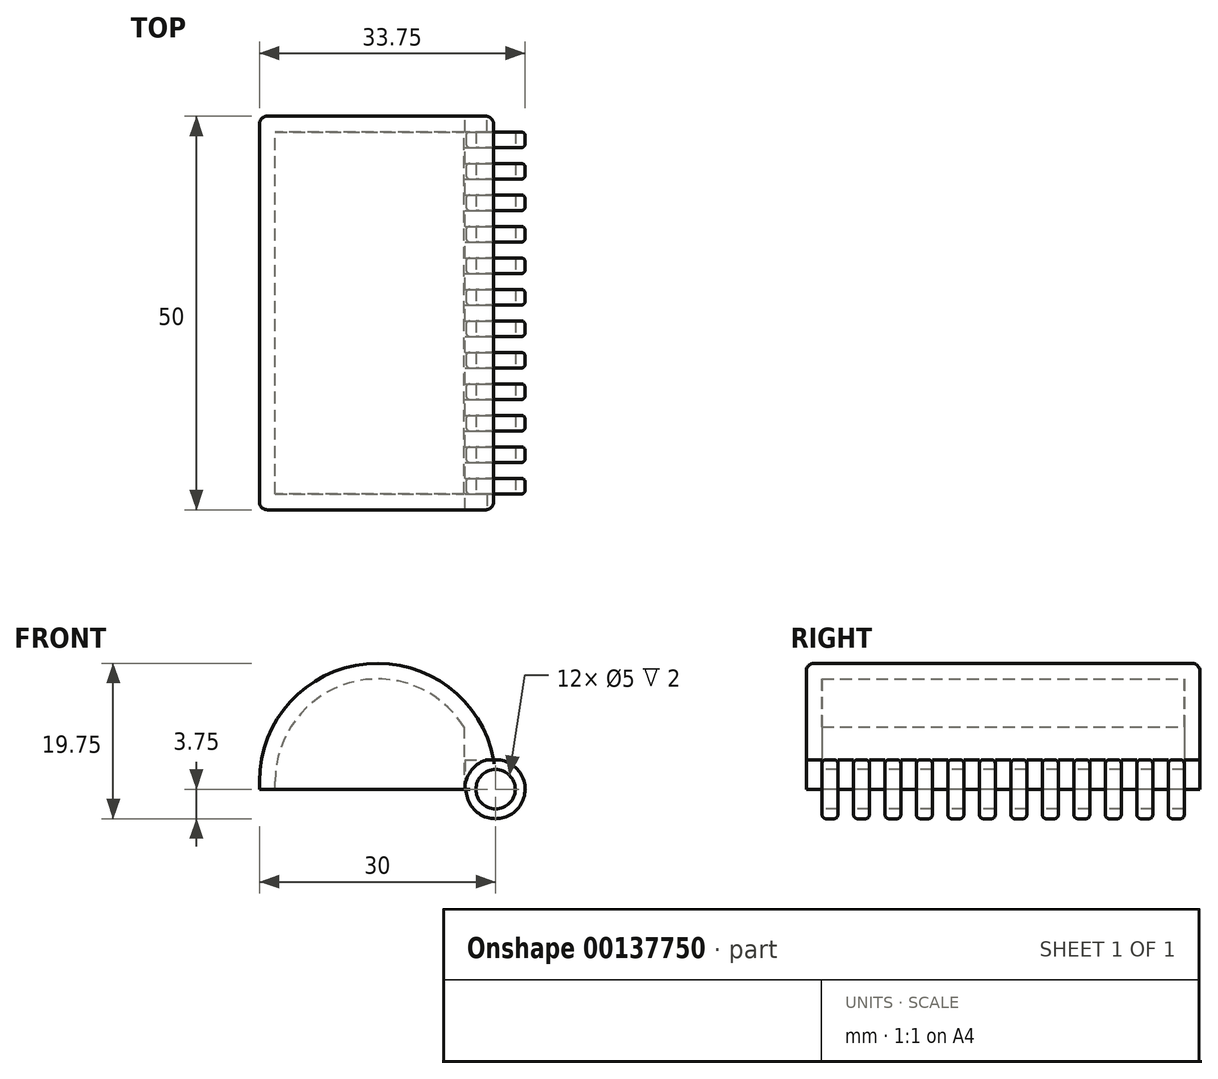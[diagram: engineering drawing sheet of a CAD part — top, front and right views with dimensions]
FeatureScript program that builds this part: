
annotation { "Feature Type Name" : "Feature", "Feature Type Description" : "" }
export const myFeature = defineFeature(function(context is Context, id is Id, definition is map)
    precondition{}
    {
        {
            var Q0;
            Q0=qCreatedBy(makeId("Front.planeOp"),FACE);
            var sketch = newSketch(context, id + "F0", { "sketchPlane" : qUnion([Q0])});
            skLineSegment(sketch, "E0.bottom", {"start": v(-15, 0) * mm, "end": v(15, 0) * mm});
            skLineSegment(sketch, "E0.left", {"start": v(-15, 0) * mm, "end": v(-15, 1) * mm});
            skLineSegment(sketch, "E0.right", {"start": v(15, 0) * mm, "end": v(15, 1) * mm});
            skArc(sketch, "E1", {"start": v(15, 1) * mm, "mid": v(0, 16) * mm, "end": v(-15, 1) * mm});
            skSolve(sketch);
        }
        {
            var Q0;
            Q0 = qSketchRegion(id + "F0", true);
            extrude(context, id + "F1", {"entities" : qUnion([Q0]), "endBound" : BoundingType.SYMMETRIC, "depth" : 50 * mm});
        }
        {
            var Q0;
            Q0=makeQuery(id+"F1.opExtrude","SWEPT_FACE",FACE,{"disambiguationData":[OSD([sQuery(id+"F0.wireOp",EDGE,"E0.bottom")])]});
            shell(context, id + "F2", {"entities" : qUnion([Q0]), "thickness" : 2 * mm});
        }
        {
            var Q0;
            Q0=qCreatedBy(makeId("Top.planeOp"),FACE);
            var sketch = newSketch(context, id + "F3", { "sketchPlane" : qUnion([Q0])});
            skLineSegment(sketch, "E2.bottom", {"start": v(11, -23) * mm, "end": v(13, -23) * mm});
            skLineSegment(sketch, "E2.top", {"start": v(11, 23) * mm, "end": v(13, 23) * mm});
            skLineSegment(sketch, "E2.left", {"start": v(11, -23) * mm, "end": v(11, 23) * mm});
            skLineSegment(sketch, "E2.right", {"start": v(13, -23) * mm, "end": v(13, 23) * mm});
            skSolve(sketch);
        }
        {
            var Q0;
            Q0 = qSketchRegion(id + "F3", true);
            extrude(context, id + "F4", {"entities" : qUnion([Q0]), "operationType" : NewBodyOperationType.ADD, "endBound" : BoundingType.UP_TO_NEXT, "depth" : 25 * mm});
        }
        {
            var Q0;
            Q0=makeQuery(id+"F1.opExtrude","CAP_FACE",FACE,{"disambiguationData":[OSD([sQuery(id+"F0.wireOp",EDGE,"E0.bottom"),sQuery(id+"F0.wireOp",EDGE,"E0.left"),sQuery(id+"F0.wireOp",EDGE,"E0.right"),sQuery(id+"F0.wireOp",EDGE,"E1")])],"isStart":false});
            var sketch = newSketch(context, id + "F5", { "sketchPlane" : qUnion([Q0])});
            skCircle(sketch, "E3", {"center": v(15, 0) * mm, "radius": 2.5 * mm});
            skCircle(sketch, "E4", {"center": v(15, 0) * mm, "radius": 3.75 * mm});
            skSolve(sketch);
        }
        {
            var Q0;
            Q0 = qSketchRegion(id + "F5", true);
            extrude(context, id + "F6", {"entities" : qUnion([Q0]), "operationType" : NewBodyOperationType.ADD, "oppositeDirection" : true, "depth" : 50 * mm});
        }
        {
            var Q0;
            Q0=makeQuery(id+"F6.boolean.opBoolean","MERGE",FACE,{"derivedFrom":[makeQuery(id+"F1.opExtrude","CAP_FACE",FACE,{"disambiguationData":[OSD([sQuery(id+"F0.wireOp",EDGE,"E0.bottom"),sQuery(id+"F0.wireOp",EDGE,"E0.left"),sQuery(id+"F0.wireOp",EDGE,"E0.right"),sQuery(id+"F0.wireOp",EDGE,"E1")])],"isStart":false}),makeQuery(id+"F6.opExtrude","CAP_FACE",FACE,{"disambiguationData":[OSD([sQuery(id+"F5.wireOp",EDGE,"E3"),sQuery(id+"F5.wireOp",EDGE,"E4")])],"isStart":true})]});
            var sketch = newSketch(context, id + "F7", { "sketchPlane" : qUnion([Q0])});
            skCircle(sketch, "E5", {"center": v(15, 0) * mm, "radius": 2.5 * mm});
            skSolve(sketch);
        }
        {
            var Q0;
            Q0 = qSketchRegion(id + "F7", true);
            extrude(context, id + "F8", {"entities" : qUnion([Q0]), "operationType" : NewBodyOperationType.REMOVE, "endBound" : BoundingType.THROUGH_ALL, "oppositeDirection" : true, "depth" : 25 * mm});
        }
        {
            var Q0;
            Q0=qCreatedBy(makeId("Right.planeOp"),FACE);
            cPlane(context, id + "F9", {"entities" : qUnion([Q0]), "cplaneType" : CPlaneType.OFFSET, "offset" : 19 * mm, "width" : 150 * mm, "height" : 150 * mm});
        }
        {
            var Q0;
            Q0=qCreatedBy(id+"F9.planeOp",FACE);
            var sketch = newSketch(context, id + "F10", { "sketchPlane" : qUnion([Q0])});
            skLineSegment(sketch, "E6.bottom", {"start": v(-25, 3.75) * mm, "end": v(-23, 3.75) * mm});
            skLineSegment(sketch, "E6.top", {"start": v(-25, -3.75) * mm, "end": v(-23, -3.75) * mm});
            skLineSegment(sketch, "E6.left", {"start": v(-25, 3.75) * mm, "end": v(-25, -3.75) * mm});
            skLineSegment(sketch, "E6.right", {"start": v(-23, 3.75) * mm, "end": v(-23, -3.75) * mm});
            skLineSegment(sketch, "E7.1.0.0", {"start": v(-19, 3.75) * mm, "end": v(-19, -3.75) * mm});
            skLineSegment(sketch, "E7.1.0.1", {"start": v(-21, 3.75) * mm, "end": v(-19, 3.75) * mm});
            skLineSegment(sketch, "E7.1.0.2", {"start": v(-21, -3.75) * mm, "end": v(-19, -3.75) * mm});
            skLineSegment(sketch, "E7.1.0.3", {"start": v(-21, 3.75) * mm, "end": v(-21, -3.75) * mm});
            skLineSegment(sketch, "E7.2.0.0", {"start": v(-15, 3.75) * mm, "end": v(-15, -3.75) * mm});
            skLineSegment(sketch, "E7.2.0.1", {"start": v(-17, 3.75) * mm, "end": v(-15, 3.75) * mm});
            skLineSegment(sketch, "E7.2.0.2", {"start": v(-17, -3.75) * mm, "end": v(-15, -3.75) * mm});
            skLineSegment(sketch, "E7.2.0.3", {"start": v(-17, 3.75) * mm, "end": v(-17, -3.75) * mm});
            skLineSegment(sketch, "E7.3.0.0", {"start": v(-11, 3.75) * mm, "end": v(-11, -3.75) * mm});
            skLineSegment(sketch, "E7.3.0.1", {"start": v(-13, 3.75) * mm, "end": v(-11, 3.75) * mm});
            skLineSegment(sketch, "E7.3.0.2", {"start": v(-13, -3.75) * mm, "end": v(-11, -3.75) * mm});
            skLineSegment(sketch, "E7.3.0.3", {"start": v(-13, 3.75) * mm, "end": v(-13, -3.75) * mm});
            skLineSegment(sketch, "E7.4.0.0", {"start": v(-7, 3.75) * mm, "end": v(-7, -3.75) * mm});
            skLineSegment(sketch, "E7.4.0.1", {"start": v(-9, 3.75) * mm, "end": v(-7, 3.75) * mm});
            skLineSegment(sketch, "E7.4.0.2", {"start": v(-9, -3.75) * mm, "end": v(-7, -3.75) * mm});
            skLineSegment(sketch, "E7.4.0.3", {"start": v(-9, 3.75) * mm, "end": v(-9, -3.75) * mm});
            skLineSegment(sketch, "E7.5.0.0", {"start": v(-3, 3.75) * mm, "end": v(-3, -3.75) * mm});
            skLineSegment(sketch, "E7.5.0.1", {"start": v(-5, 3.75) * mm, "end": v(-3, 3.75) * mm});
            skLineSegment(sketch, "E7.5.0.2", {"start": v(-5, -3.75) * mm, "end": v(-3, -3.75) * mm});
            skLineSegment(sketch, "E7.5.0.3", {"start": v(-5, 3.75) * mm, "end": v(-5, -3.75) * mm});
            skLineSegment(sketch, "E7.6.0.0", {"start": v(1, 3.75) * mm, "end": v(1, -3.75) * mm});
            skLineSegment(sketch, "E7.6.0.1", {"start": v(-1, 3.75) * mm, "end": v(1, 3.75) * mm});
            skLineSegment(sketch, "E7.6.0.2", {"start": v(-1, -3.75) * mm, "end": v(1, -3.75) * mm});
            skLineSegment(sketch, "E7.6.0.3", {"start": v(-1, 3.75) * mm, "end": v(-1, -3.75) * mm});
            skLineSegment(sketch, "E7.7.0.0", {"start": v(5, 3.75) * mm, "end": v(5, -3.75) * mm});
            skLineSegment(sketch, "E7.7.0.1", {"start": v(3, 3.75) * mm, "end": v(5, 3.75) * mm});
            skLineSegment(sketch, "E7.7.0.2", {"start": v(3, -3.75) * mm, "end": v(5, -3.75) * mm});
            skLineSegment(sketch, "E7.7.0.3", {"start": v(3, 3.75) * mm, "end": v(3, -3.75) * mm});
            skLineSegment(sketch, "E7.8.0.0", {"start": v(9, 3.75) * mm, "end": v(9, -3.75) * mm});
            skLineSegment(sketch, "E7.8.0.1", {"start": v(7, 3.75) * mm, "end": v(9, 3.75) * mm});
            skLineSegment(sketch, "E7.8.0.2", {"start": v(7, -3.75) * mm, "end": v(9, -3.75) * mm});
            skLineSegment(sketch, "E7.8.0.3", {"start": v(7, 3.75) * mm, "end": v(7, -3.75) * mm});
            skLineSegment(sketch, "E7.9.0.0", {"start": v(13, 3.75) * mm, "end": v(13, -3.75) * mm});
            skLineSegment(sketch, "E7.9.0.1", {"start": v(11, 3.75) * mm, "end": v(13, 3.75) * mm});
            skLineSegment(sketch, "E7.9.0.2", {"start": v(11, -3.75) * mm, "end": v(13, -3.75) * mm});
            skLineSegment(sketch, "E7.9.0.3", {"start": v(11, 3.75) * mm, "end": v(11, -3.75) * mm});
            skLineSegment(sketch, "E7.10.0.0", {"start": v(17, 3.75) * mm, "end": v(17, -3.75) * mm});
            skLineSegment(sketch, "E7.10.0.1", {"start": v(15, 3.75) * mm, "end": v(17, 3.75) * mm});
            skLineSegment(sketch, "E7.10.0.2", {"start": v(15, -3.75) * mm, "end": v(17, -3.75) * mm});
            skLineSegment(sketch, "E7.10.0.3", {"start": v(15, 3.75) * mm, "end": v(15, -3.75) * mm});
            skLineSegment(sketch, "E7.11.0.0", {"start": v(21, 3.75) * mm, "end": v(21, -3.75) * mm});
            skLineSegment(sketch, "E7.11.0.1", {"start": v(19, 3.75) * mm, "end": v(21, 3.75) * mm});
            skLineSegment(sketch, "E7.11.0.2", {"start": v(19, -3.75) * mm, "end": v(21, -3.75) * mm});
            skLineSegment(sketch, "E7.11.0.3", {"start": v(19, 3.75) * mm, "end": v(19, -3.75) * mm});
            skLineSegment(sketch, "E7.direction1", {"start": v(-23, -3.75) * mm, "end": v(-19, -3.75) * mm, "construction": true});
            skLineSegment(sketch, "E8.0.12.0", {"start": v(25, 3.75) * mm, "end": v(25, -3.75) * mm});
            skLineSegment(sketch, "E8.3.12.0", {"start": v(23, 3.75) * mm, "end": v(25, 3.75) * mm});
            skLineSegment(sketch, "E8.6.12.0", {"start": v(23, -3.75) * mm, "end": v(25, -3.75) * mm});
            skLineSegment(sketch, "E8.9.12.0", {"start": v(23, 3.75) * mm, "end": v(23, -3.75) * mm});
            skSolve(sketch);
        }
        {
            var Q0;
            Q0 = qSketchRegion(id + "F10", true);
            extrude(context, id + "F11", {"entities" : qUnion([Q0]), "operationType" : NewBodyOperationType.REMOVE, "oppositeDirection" : true, "depth" : 7.9 * mm});
        }
        {
            var Q0;
            Q0=makeQuery(id+"F11.boolean.opBoolean","INTERSECT",EDGE,{"derivedFrom":[makeQuery(id+"F6.opExtrude","SWEPT_FACE",FACE,{"disambiguationData":[OSD([sQuery(id+"F5.wireOp",EDGE,"E4")])]}),makeQuery(id+"F11.opExtrude","SWEPT_FACE",FACE,{"disambiguationData":[OSD([sQuery(id+"F10.wireOp",EDGE,"E7.1.0.3")])]})]});
            var Q1;
            Q1=makeQuery(id+"F11.boolean.opBoolean","INTERSECT",EDGE,{"derivedFrom":[makeQuery(id+"F6.opExtrude","SWEPT_FACE",FACE,{"disambiguationData":[OSD([sQuery(id+"F5.wireOp",EDGE,"E4")])]}),makeQuery(id+"F11.opExtrude","SWEPT_FACE",FACE,{"disambiguationData":[OSD([sQuery(id+"F10.wireOp",EDGE,"E7.1.0.0")])]})]});
            var Q2;
            Q2=makeQuery(id+"F11.boolean.opBoolean","INTERSECT",EDGE,{"derivedFrom":[makeQuery(id+"F6.opExtrude","SWEPT_FACE",FACE,{"disambiguationData":[OSD([sQuery(id+"F5.wireOp",EDGE,"E4")])]}),makeQuery(id+"F11.opExtrude","SWEPT_FACE",FACE,{"disambiguationData":[OSD([sQuery(id+"F10.wireOp",EDGE,"E7.2.0.3")])]})]});
            var Q3;
            Q3=makeQuery(id+"F11.boolean.opBoolean","INTERSECT",EDGE,{"derivedFrom":[makeQuery(id+"F6.opExtrude","SWEPT_FACE",FACE,{"disambiguationData":[OSD([sQuery(id+"F5.wireOp",EDGE,"E4")])]}),makeQuery(id+"F11.opExtrude","SWEPT_FACE",FACE,{"disambiguationData":[OSD([sQuery(id+"F10.wireOp",EDGE,"E7.2.0.0")])]})]});
            var Q4;
            Q4=makeQuery(id+"F11.boolean.opBoolean","INTERSECT",EDGE,{"derivedFrom":[makeQuery(id+"F6.opExtrude","SWEPT_FACE",FACE,{"disambiguationData":[OSD([sQuery(id+"F5.wireOp",EDGE,"E4")])]}),makeQuery(id+"F11.opExtrude","SWEPT_FACE",FACE,{"disambiguationData":[OSD([sQuery(id+"F10.wireOp",EDGE,"E7.3.0.3")])]})]});
            var Q5;
            Q5=makeQuery(id+"F11.boolean.opBoolean","INTERSECT",EDGE,{"derivedFrom":[makeQuery(id+"F6.opExtrude","SWEPT_FACE",FACE,{"disambiguationData":[OSD([sQuery(id+"F5.wireOp",EDGE,"E4")])]}),makeQuery(id+"F11.opExtrude","SWEPT_FACE",FACE,{"disambiguationData":[OSD([sQuery(id+"F10.wireOp",EDGE,"E7.3.0.0")])]})]});
            var Q6;
            Q6=makeQuery(id+"F11.boolean.opBoolean","INTERSECT",EDGE,{"derivedFrom":[makeQuery(id+"F6.opExtrude","SWEPT_FACE",FACE,{"disambiguationData":[OSD([sQuery(id+"F5.wireOp",EDGE,"E4")])]}),makeQuery(id+"F11.opExtrude","SWEPT_FACE",FACE,{"disambiguationData":[OSD([sQuery(id+"F10.wireOp",EDGE,"E7.4.0.3")])]})]});
            var Q7;
            Q7=makeQuery(id+"F11.boolean.opBoolean","INTERSECT",EDGE,{"derivedFrom":[makeQuery(id+"F6.opExtrude","SWEPT_FACE",FACE,{"disambiguationData":[OSD([sQuery(id+"F5.wireOp",EDGE,"E4")])]}),makeQuery(id+"F11.opExtrude","SWEPT_FACE",FACE,{"disambiguationData":[OSD([sQuery(id+"F10.wireOp",EDGE,"E7.4.0.0")])]})]});
            var Q8;
            Q8=makeQuery(id+"F11.boolean.opBoolean","INTERSECT",EDGE,{"derivedFrom":[makeQuery(id+"F6.opExtrude","SWEPT_FACE",FACE,{"disambiguationData":[OSD([sQuery(id+"F5.wireOp",EDGE,"E4")])]}),makeQuery(id+"F11.opExtrude","SWEPT_FACE",FACE,{"disambiguationData":[OSD([sQuery(id+"F10.wireOp",EDGE,"E7.5.0.3")])]})]});
            var Q9;
            Q9=makeQuery(id+"F11.boolean.opBoolean","INTERSECT",EDGE,{"derivedFrom":[makeQuery(id+"F6.opExtrude","SWEPT_FACE",FACE,{"disambiguationData":[OSD([sQuery(id+"F5.wireOp",EDGE,"E4")])]}),makeQuery(id+"F11.opExtrude","SWEPT_FACE",FACE,{"disambiguationData":[OSD([sQuery(id+"F10.wireOp",EDGE,"E7.5.0.0")])]})]});
            var Q10;
            Q10=makeQuery(id+"F11.boolean.opBoolean","INTERSECT",EDGE,{"derivedFrom":[makeQuery(id+"F6.opExtrude","SWEPT_FACE",FACE,{"disambiguationData":[OSD([sQuery(id+"F5.wireOp",EDGE,"E4")])]}),makeQuery(id+"F11.opExtrude","SWEPT_FACE",FACE,{"disambiguationData":[OSD([sQuery(id+"F10.wireOp",EDGE,"E7.6.0.3")])]})]});
            var Q11;
            Q11=makeQuery(id+"F11.boolean.opBoolean","INTERSECT",EDGE,{"derivedFrom":[makeQuery(id+"F6.opExtrude","SWEPT_FACE",FACE,{"disambiguationData":[OSD([sQuery(id+"F5.wireOp",EDGE,"E4")])]}),makeQuery(id+"F11.opExtrude","SWEPT_FACE",FACE,{"disambiguationData":[OSD([sQuery(id+"F10.wireOp",EDGE,"E7.6.0.0")])]})]});
            var Q12;
            Q12=makeQuery(id+"F11.boolean.opBoolean","INTERSECT",EDGE,{"derivedFrom":[makeQuery(id+"F6.opExtrude","SWEPT_FACE",FACE,{"disambiguationData":[OSD([sQuery(id+"F5.wireOp",EDGE,"E4")])]}),makeQuery(id+"F11.opExtrude","SWEPT_FACE",FACE,{"disambiguationData":[OSD([sQuery(id+"F10.wireOp",EDGE,"E7.7.0.3")])]})]});
            var Q13;
            Q13=makeQuery(id+"F11.boolean.opBoolean","INTERSECT",EDGE,{"derivedFrom":[makeQuery(id+"F6.opExtrude","SWEPT_FACE",FACE,{"disambiguationData":[OSD([sQuery(id+"F5.wireOp",EDGE,"E4")])]}),makeQuery(id+"F11.opExtrude","SWEPT_FACE",FACE,{"disambiguationData":[OSD([sQuery(id+"F10.wireOp",EDGE,"E7.7.0.0")])]})]});
            var Q14;
            Q14=makeQuery(id+"F11.boolean.opBoolean","INTERSECT",EDGE,{"derivedFrom":[makeQuery(id+"F6.opExtrude","SWEPT_FACE",FACE,{"disambiguationData":[OSD([sQuery(id+"F5.wireOp",EDGE,"E4")])]}),makeQuery(id+"F11.opExtrude","SWEPT_FACE",FACE,{"disambiguationData":[OSD([sQuery(id+"F10.wireOp",EDGE,"E7.8.0.3")])]})]});
            var Q15;
            Q15=makeQuery(id+"F11.boolean.opBoolean","INTERSECT",EDGE,{"derivedFrom":[makeQuery(id+"F6.opExtrude","SWEPT_FACE",FACE,{"disambiguationData":[OSD([sQuery(id+"F5.wireOp",EDGE,"E4")])]}),makeQuery(id+"F11.opExtrude","SWEPT_FACE",FACE,{"disambiguationData":[OSD([sQuery(id+"F10.wireOp",EDGE,"E7.8.0.0")])]})]});
            var Q16;
            Q16=makeQuery(id+"F11.boolean.opBoolean","INTERSECT",EDGE,{"derivedFrom":[makeQuery(id+"F6.opExtrude","SWEPT_FACE",FACE,{"disambiguationData":[OSD([sQuery(id+"F5.wireOp",EDGE,"E4")])]}),makeQuery(id+"F11.opExtrude","SWEPT_FACE",FACE,{"disambiguationData":[OSD([sQuery(id+"F10.wireOp",EDGE,"E7.9.0.3")])]})]});
            var Q17;
            Q17=makeQuery(id+"F11.boolean.opBoolean","INTERSECT",EDGE,{"derivedFrom":[makeQuery(id+"F6.opExtrude","SWEPT_FACE",FACE,{"disambiguationData":[OSD([sQuery(id+"F5.wireOp",EDGE,"E4")])]}),makeQuery(id+"F11.opExtrude","SWEPT_FACE",FACE,{"disambiguationData":[OSD([sQuery(id+"F10.wireOp",EDGE,"E7.9.0.0")])]})]});
            var Q18;
            Q18=makeQuery(id+"F11.boolean.opBoolean","INTERSECT",EDGE,{"derivedFrom":[makeQuery(id+"F6.opExtrude","SWEPT_FACE",FACE,{"disambiguationData":[OSD([sQuery(id+"F5.wireOp",EDGE,"E4")])]}),makeQuery(id+"F11.opExtrude","SWEPT_FACE",FACE,{"disambiguationData":[OSD([sQuery(id+"F10.wireOp",EDGE,"E7.10.0.3")])]})]});
            var Q19;
            Q19=makeQuery(id+"F11.boolean.opBoolean","INTERSECT",EDGE,{"derivedFrom":[makeQuery(id+"F6.opExtrude","SWEPT_FACE",FACE,{"disambiguationData":[OSD([sQuery(id+"F5.wireOp",EDGE,"E4")])]}),makeQuery(id+"F11.opExtrude","SWEPT_FACE",FACE,{"disambiguationData":[OSD([sQuery(id+"F10.wireOp",EDGE,"E7.10.0.0")])]})]});
            var Q20;
            Q20=makeQuery(id+"F11.boolean.opBoolean","INTERSECT",EDGE,{"derivedFrom":[makeQuery(id+"F6.opExtrude","SWEPT_FACE",FACE,{"disambiguationData":[OSD([sQuery(id+"F5.wireOp",EDGE,"E4")])]}),makeQuery(id+"F11.opExtrude","SWEPT_FACE",FACE,{"disambiguationData":[OSD([sQuery(id+"F10.wireOp",EDGE,"E7.11.0.3")])]})]});
            var Q21;
            Q21=makeQuery(id+"F11.boolean.opBoolean","INTERSECT",EDGE,{"derivedFrom":[makeQuery(id+"F6.opExtrude","SWEPT_FACE",FACE,{"disambiguationData":[OSD([sQuery(id+"F5.wireOp",EDGE,"E4")])]}),makeQuery(id+"F11.opExtrude","SWEPT_FACE",FACE,{"disambiguationData":[OSD([sQuery(id+"F10.wireOp",EDGE,"E7.11.0.0")])]})]});
            var Q22;
            Q22=makeQuery(id+"F11.boolean.opBoolean","INTERSECT",EDGE,{"derivedFrom":[makeQuery(id+"F6.opExtrude","SWEPT_FACE",FACE,{"disambiguationData":[OSD([sQuery(id+"F5.wireOp",EDGE,"E4")])]}),makeQuery(id+"F11.opExtrude","SWEPT_FACE",FACE,{"disambiguationData":[OSD([sQuery(id+"F10.wireOp",EDGE,"E8.9.12.0")])]})]});
            var Q23;
            Q23=makeQuery(id+"F11.boolean.opBoolean","INTERSECT",EDGE,{"derivedFrom":[makeQuery(id+"F6.opExtrude","SWEPT_FACE",FACE,{"disambiguationData":[OSD([sQuery(id+"F5.wireOp",EDGE,"E4")])]}),makeQuery(id+"F11.opExtrude","SWEPT_FACE",FACE,{"disambiguationData":[OSD([sQuery(id+"F10.wireOp",EDGE,"E6.right")])]})]});
            fillet(context, id + "F12", {"entities" : qUnion([Q0, Q1, Q2, Q3, Q4, Q5, Q6, Q7, Q8, Q9, Q10, Q11, Q12, Q13, Q14, Q15, Q16, Q17, Q18, Q19, Q20, Q21, Q22, Q23]), "radius" : .5 * mm, "tangentPropagation" : true, "allowEdgeOverflow" : false});
        }
        {
            var Q0;
            Q0=makeQuery(id+"F6.boolean.opBoolean","MERGE",FACE,{"derivedFrom":[makeQuery(id+"F1.opExtrude","CAP_FACE",FACE,{"disambiguationData":[OSD([sQuery(id+"F0.wireOp",EDGE,"E0.bottom"),sQuery(id+"F0.wireOp",EDGE,"E0.left"),sQuery(id+"F0.wireOp",EDGE,"E0.right"),sQuery(id+"F0.wireOp",EDGE,"E1")])],"isStart":false}),makeQuery(id+"F6.opExtrude","CAP_FACE",FACE,{"disambiguationData":[OSD([sQuery(id+"F5.wireOp",EDGE,"E3"),sQuery(id+"F5.wireOp",EDGE,"E4")])],"isStart":true})]});
            var sketch = newSketch(context, id + "F13", { "sketchPlane" : qUnion([Q0])});
            skArc(sketch, "E9", {"start": v(13.93, 3.75) * mm, "mid": v(11.89, 2.35) * mm, "end": v(11.1, 0) * mm});
            skLineSegment(sketch, "E10", {"start": v(11.1, 0) * mm, "end": v(11.1, 3.75) * mm});
            skLineSegment(sketch, "E11", {"start": v(11.1, 3.75) * mm, "end": v(13.93, 3.75) * mm});
            skSolve(sketch);
        }
        {
            var Q0;
            Q0 = qSketchRegion(id + "F13", true);
            var Q1;
            Q1=makeQuery(id+"F11.boolean.opBoolean","COPY",FACE,{"derivedFrom":makeQuery(id+"F11.opExtrude","SWEPT_FACE",FACE,{"disambiguationData":[OSD([sQuery(id+"F10.wireOp",EDGE,"E6.right")])]})});
            extrude(context, id + "F14", {"entities" : qUnion([Q0]), "operationType" : NewBodyOperationType.ADD, "oppositeDirection" : true, "endBoundEntityFace" : qUnion([Q1]), "depth" : 2.1 * mm});
        }
        {
            var Q0;
            Q0=makeQuery(id+"F6.boolean.opBoolean","MERGE",FACE,{"derivedFrom":[makeQuery(id+"F1.opExtrude","CAP_FACE",FACE,{"disambiguationData":[OSD([sQuery(id+"F0.wireOp",EDGE,"E0.bottom"),sQuery(id+"F0.wireOp",EDGE,"E0.left"),sQuery(id+"F0.wireOp",EDGE,"E0.right"),sQuery(id+"F0.wireOp",EDGE,"E1")])],"isStart":true}),makeQuery(id+"F6.opExtrude","CAP_FACE",FACE,{"disambiguationData":[OSD([sQuery(id+"F5.wireOp",EDGE,"E3"),sQuery(id+"F5.wireOp",EDGE,"E4")])],"isStart":false})]});
            var sketch = newSketch(context, id + "F15", { "sketchPlane" : qUnion([Q0])});
            skArc(sketch, "E12", {"start": v(-11.1, 0) * mm, "mid": v(-11.89, 2.35) * mm, "end": v(-13.93, 3.75) * mm});
            skLineSegment(sketch, "E13", {"start": v(-13.93, 3.75) * mm, "end": v(-11.1, 3.75) * mm});
            skLineSegment(sketch, "E14", {"start": v(-11.1, 3.75) * mm, "end": v(-11.1, 0) * mm});
            skSolve(sketch);
        }
        {
            var Q0;
            Q0 = qSketchRegion(id + "F15", true);
            extrude(context, id + "F16", {"entities" : qUnion([Q0]), "operationType" : NewBodyOperationType.ADD, "oppositeDirection" : true, "depth" : 2.3 * mm});
        }
        {
            var Q0;
            {var subQ1=sQuery(id+"F0.wireOp",EDGE,"E1");var subQ2=sQuery(id+"F0.wireOp",EDGE,"E0.left");Q0=makeQuery(id+"F6.boolean.opBoolean","SPLIT",EDGE,{"disambiguationData":[TD([makeQuery(id+"F1.opExtrude","SWEPT_FACE",FACE,{"disambiguationData":[OSD([subQ2])]})])],"derivedFrom":makeQuery(id+"F1.opExtrude","CAP_EDGE",EDGE,{"disambiguationData":[OSD([subQ1])],"isStart":false})});}
            var Q1;
            {var subQ0=sQuery(id+"F0.wireOp",EDGE,"E1");var subQ1=sQuery(id+"F0.wireOp",EDGE,"E0.left");Q1=makeQuery(id+"F6.boolean.opBoolean","SPLIT",EDGE,{"disambiguationData":[TD([makeQuery(id+"F1.opExtrude","SWEPT_FACE",FACE,{"disambiguationData":[OSD([subQ1])]})])],"derivedFrom":makeQuery(id+"F1.opExtrude","CAP_EDGE",EDGE,{"disambiguationData":[OSD([subQ0])],"isStart":true})});}
            fillet(context, id + "F17", {"entities" : qUnion([Q0, Q1]), "radius" : 1 * mm, "tangentPropagation" : true, "allowEdgeOverflow" : false});
        }
    });
